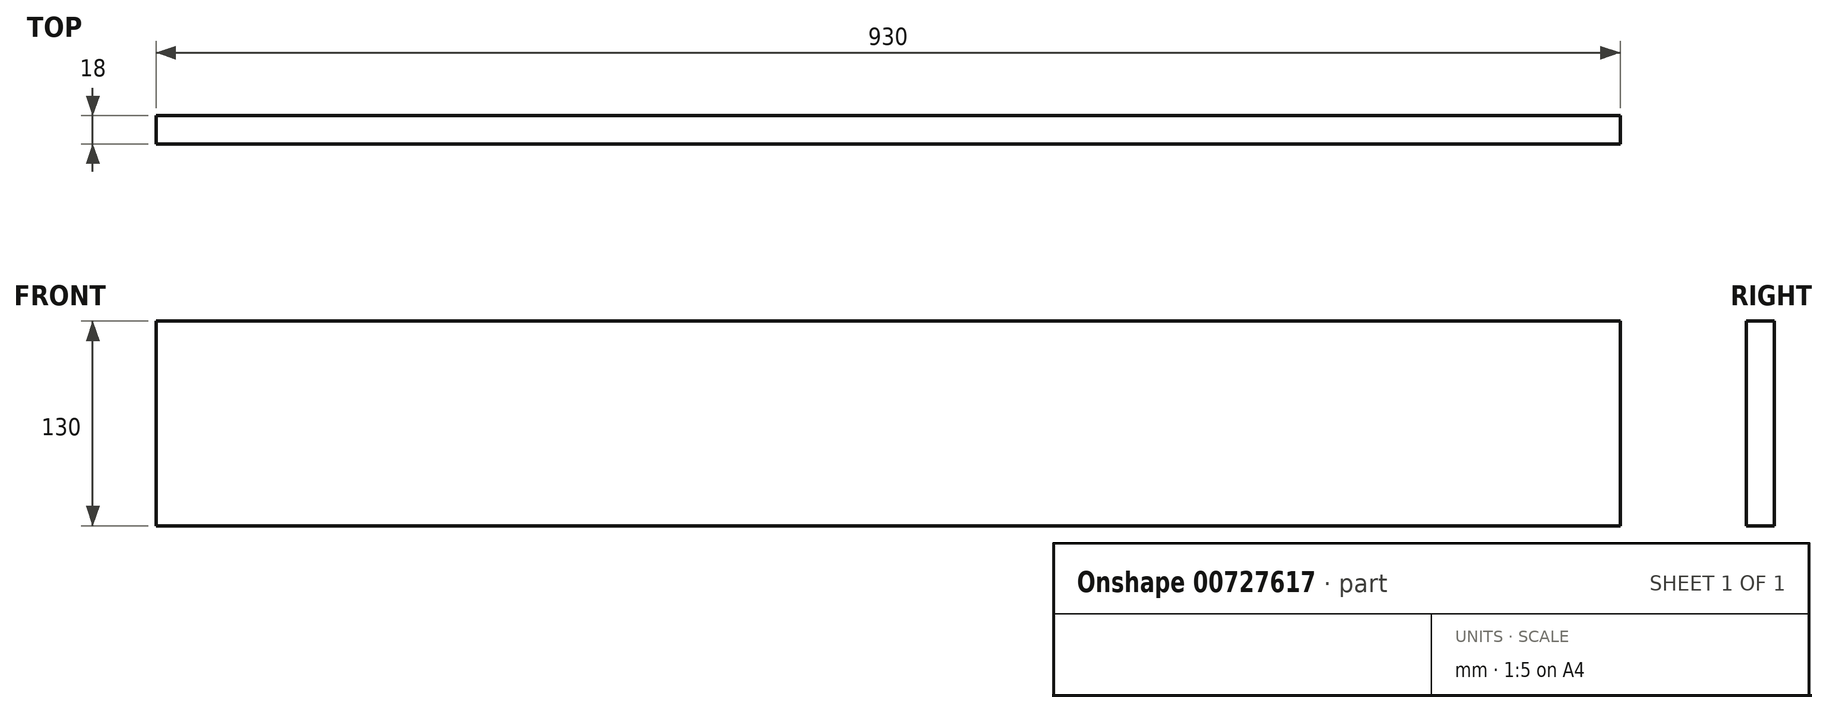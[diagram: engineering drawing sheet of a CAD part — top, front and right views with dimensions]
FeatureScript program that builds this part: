
annotation { "Feature Type Name" : "Feature", "Feature Type Description" : "" }
export const myFeature = defineFeature(function(context is Context, id is Id, definition is map)
    precondition{}
    {
        {
            var Q0;
            Q0=qCreatedBy(makeId("Front.planeOp"),FACE);
            var sketch = newSketch(context, id + "F0", { "sketchPlane" : qUnion([Q0])});
            skLineSegment(sketch, "E0.bottom", {"start": v(-465, 65) * mm, "end": v(465, 65) * mm});
            skLineSegment(sketch, "E0.top", {"start": v(-465, -65) * mm, "end": v(465, -65) * mm});
            skLineSegment(sketch, "E0.left", {"start": v(-465, 65) * mm, "end": v(-465, -65) * mm});
            skLineSegment(sketch, "E0.right", {"start": v(465, 65) * mm, "end": v(465, -65) * mm});
            skLineSegment(sketch, "E1", {"start": v(-465, 65) * mm, "end": v(465, -65) * mm, "construction": true});
            skSolve(sketch);
        }
        {
            var Q0;
            Q0 = qSketchRegion(id + "F0", true);
            extrude(context, id + "F1", {"entities" : qUnion([Q0]), "oppositeDirection" : true, "depth" : 18 * mm, "offsetDistance" : 25 * mm});
        }
    });
